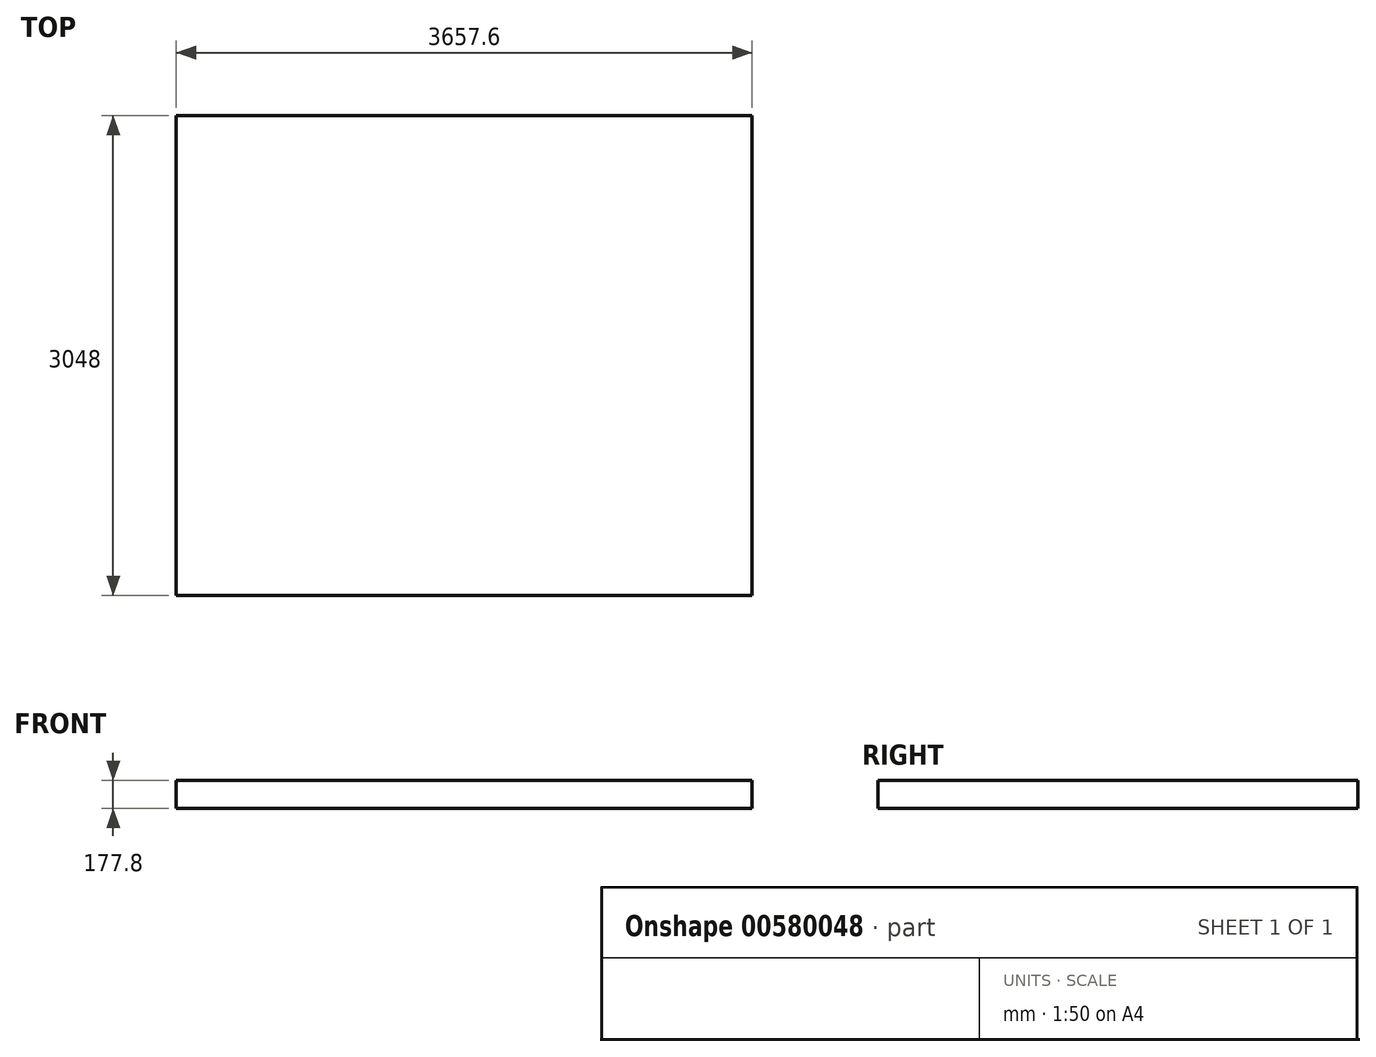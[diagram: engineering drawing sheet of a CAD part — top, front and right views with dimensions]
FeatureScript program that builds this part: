
annotation { "Feature Type Name" : "Feature", "Feature Type Description" : "" }
export const myFeature = defineFeature(function(context is Context, id is Id, definition is map)
    precondition{}
    {
        {
            var Q0;
            Q0=qCreatedBy(makeId("Top.planeOp"),FACE);
            var sketch = newSketch(context, id + "F0", { "sketchPlane" : qUnion([Q0])});
            skLineSegment(sketch, "E0.bottom", {"start": v(-1835.56, 2109.79) * mm, "end": v(1822.04, 2109.79) * mm});
            skLineSegment(sketch, "E0.top", {"start": v(-1835.56, -938.21) * mm, "end": v(1822.04, -938.21) * mm});
            skLineSegment(sketch, "E0.left", {"start": v(-1835.56, 2109.79) * mm, "end": v(-1835.56, -938.21) * mm});
            skLineSegment(sketch, "E0.right", {"start": v(1822.04, 2109.79) * mm, "end": v(1822.04, -938.21) * mm});
            skSolve(sketch);
        }
        {
            var Q0;
            Q0 = qSketchRegion(id + "F0", true);
            extrude(context, id + "F1", {"entities" : qUnion([Q0]), "depth" : 177.8 * mm, "offsetDistance" : 30.48 * mm});
        }
    });
